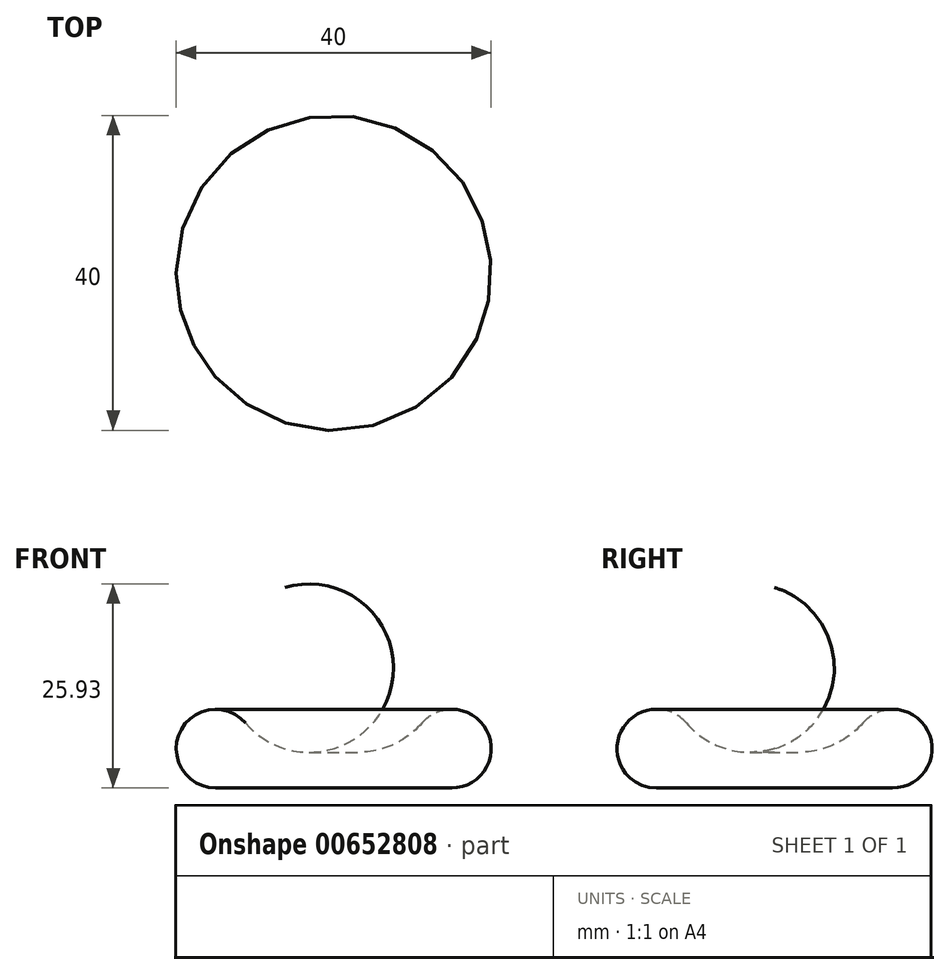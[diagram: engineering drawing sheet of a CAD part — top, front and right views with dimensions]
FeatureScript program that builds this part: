
annotation { "Feature Type Name" : "Feature", "Feature Type Description" : "" }
export const myFeature = defineFeature(function(context is Context, id is Id, definition is map)
    precondition{}
    {
        {
            var Q0;
            Q0=qCreatedBy(makeId("Front.planeOp"),FACE);
            var sketch = newSketch(context, id + "F0", { "sketchPlane" : qUnion([Q0])});
            skArc(sketch, "E0", {"start": v(-11.2, 8.26) * mm, "mid": v(-19.54, 7.09) * mm, "end": v(-15, 0) * mm});
            skArc(sketch, "E1", {"start": v(-11.2, 8.26) * mm, "mid": v(-6.09, 4.97) * mm, "end": v(0, 5) * mm});
            skLineSegment(sketch, "E2", {"start": v(0, 0) * mm, "end": v(-15, 0) * mm});
            skLineSegment(sketch, "E3", {"start": v(0, 0) * mm, "end": v(0, 5) * mm});
            skSolve(sketch);
        }
        {
            var Q0;
            Q0=makeQuery(id+"F0.imprint","IMPRINT",FACE,{"disambiguationData":[TD([[makeQuery(id+"F0.imprint","IMPRINT",EDGE,{"derivedFrom":sQuery(id+"F0.wireOp",EDGE,"E0")}),1.0]])]});
            var sketch = newSketch(context, id + "F1", { "sketchPlane" : qUnion([Q0])});
            skSolve(sketch);
        }
        {
            var Q0;
            Q0 = qSketchRegion(id + "F1", true);
            var Q1;
            Q1=makeQuery(id+"F0.imprint","IMPRINT",FACE,{"disambiguationData":[TD([[makeQuery(id+"F0.imprint","IMPRINT",EDGE,{"derivedFrom":sQuery(id+"F0.wireOp",EDGE,"E0")}),1.0]])]});
            var Q2;
            Q2=sQuery(id+"F0.wireOp",EDGE,"E3");
            revolve(context, id + "F2", {"entities" : qUnion([Q0, Q1]), "axis" : qUnion([Q2]), "revolveType" : RevolveType.FULL});
        }
        {
            var Q0;
            Q0=qCreatedBy(makeId("Top.planeOp"),FACE);
            cPlane(context, id + "F3", {"entities" : qUnion([Q0]), "cplaneType" : CPlaneType.OFFSET, "offset" : 5 * mm, "width" : 150 * mm, "height" : 150 * mm});
        }
    });
